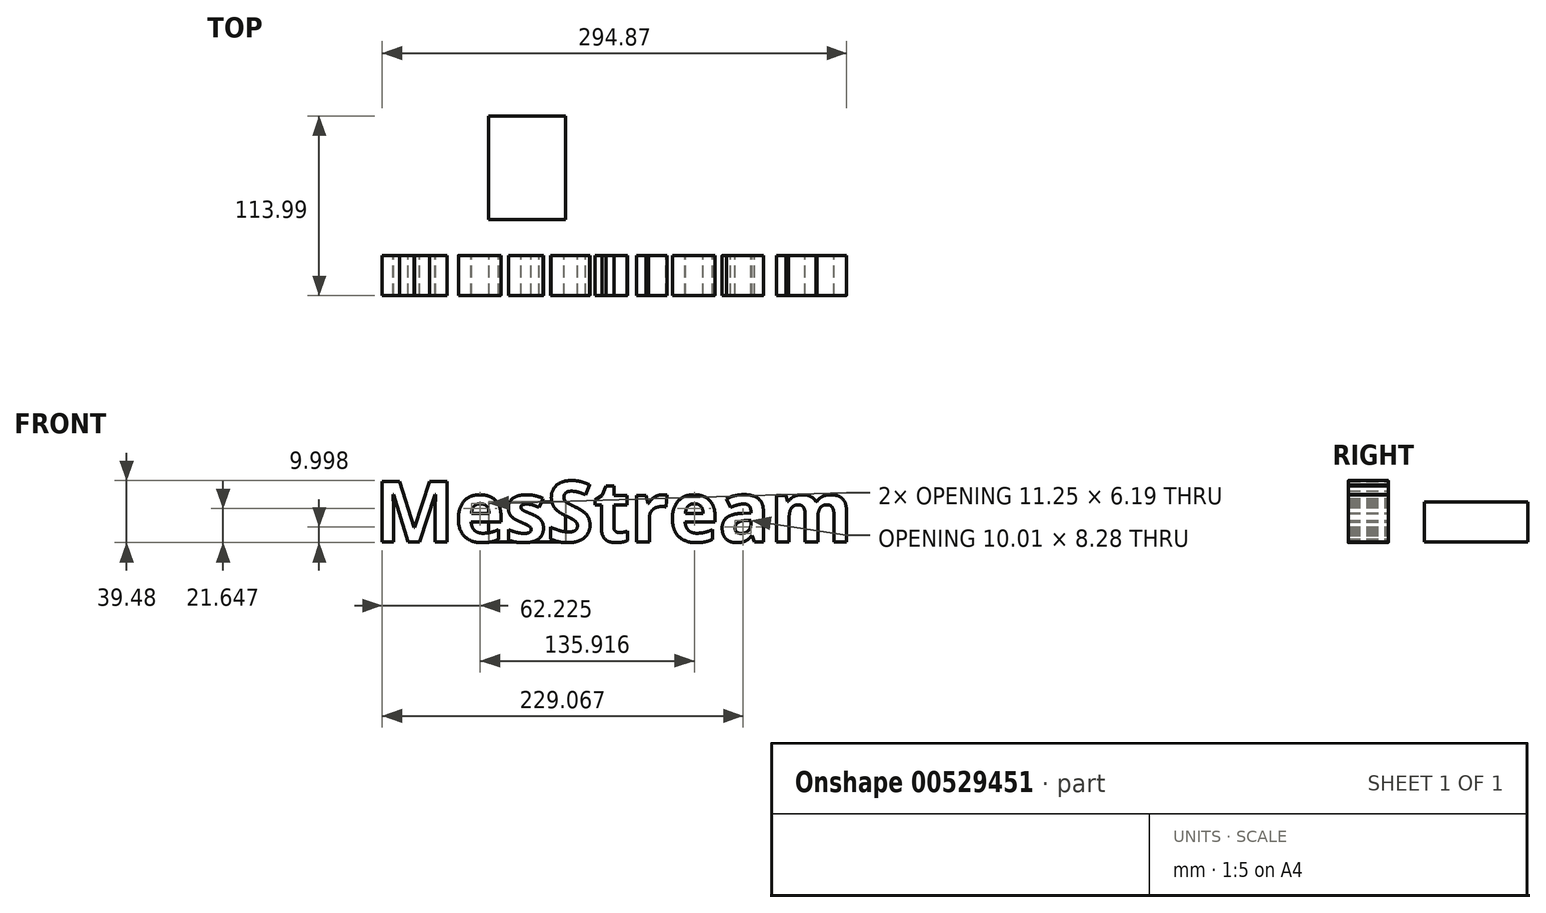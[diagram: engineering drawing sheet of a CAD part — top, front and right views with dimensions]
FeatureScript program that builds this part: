
annotation { "Feature Type Name" : "Feature", "Feature Type Description" : "" }
export const myFeature = defineFeature(function(context is Context, id is Id, definition is map)
    precondition{}
    {
        {
            var Q0;
            Q0=qCreatedBy(makeId("Top.planeOp"),FACE);
            var sketch = newSketch(context, id + "F0", { "sketchPlane" : qUnion([Q0])});
            skLineSegment(sketch, "E0.bottom", {"start": v(55.5, 63.19) * mm, "end": v(32.27, 63.19) * mm});
            skLineSegment(sketch, "E0.top", {"start": v(55.5, 22.94) * mm, "end": v(32.27, 22.94) * mm});
            skLineSegment(sketch, "E0.left", {"start": v(55.5, 63.19) * mm, "end": v(55.5, 22.94) * mm});
            skLineSegment(sketch, "E0.right", {"start": v(32.27, 63.19) * mm, "end": v(32.27, 22.94) * mm});
            skSolve(sketch);
        }
        {
            var Q0;
            Q0=makeQuery(id+"F0.imprint","IMPRINT",FACE,{"disambiguationData":[TD([[makeQuery(id+"F0.imprint","IMPRINT",EDGE,{"derivedFrom":sQuery(id+"F0.wireOp",EDGE,"E0.bottom")}),1.0]])]});
            extrude(context, id + "F1", {"entities" : qUnion([Q0]), "depth" : 25.4 * mm, "offsetDistance" : 25.4 * mm});
        }
        {
            var Q0;
            Q0=makeQuery(id+"F1.opExtrude","SWEPT_FACE",FACE,{"disambiguationData":[OSD([sQuery(id+"F0.wireOp",EDGE,"E0.left")])]});
            extrude(context, id + "F2", {"entities" : qUnion([Q0]), "operationType" : NewBodyOperationType.ADD, "depth" : 25.4 * mm, "offsetDistance" : 25.4 * mm});
        }
        {
            var Q0;
            {var subQ0=sQuery(id+"F0.wireOp",EDGE,"E0.bottom");Q0=makeQuery(id+"F2.boolean.opBoolean","MERGE",FACE,{"derivedFrom":[makeQuery(id+"F1.opExtrude","SWEPT_FACE",FACE,{"disambiguationData":[OSD([subQ0])]}),makeQuery(id+"F2.opExtrude","SWEPT_FACE",FACE,{"disambiguationData":[OSD([subQ0,sQuery(id+"F0.wireOp",EDGE,"E0.left")])]})]});}
            extrude(context, id + "F3", {"entities" : qUnion([Q0]), "operationType" : NewBodyOperationType.ADD, "depth" : 25.4 * mm, "offsetDistance" : 25.4 * mm});
        }
        {
            var Q0;
            Q0=qCreatedBy(makeId("Front.planeOp"),FACE);
            var sketch = newSketch(context, id + "F4", { "sketchPlane" : qUnion([Q0])});
            skText(sketch, "E1", { "text": "MesStream", "fontName": "OpenSans-Bold.ttf"});
            const initialGuessF4  = {"E1": [-0.04018, 0, 1, 0, 0.03873]};
            skSetInitialGuess(sketch, initialGuessF4);
            skSolve(sketch);
        }
        {
            var Q0;
            Q0 = qSketchRegion(id + "F4", true);
            extrude(context, id + "F5", {"entities" : qUnion([Q0]), "depth" : 25.4 * mm, "offsetDistance" : 25.4 * mm});
        }
    });
